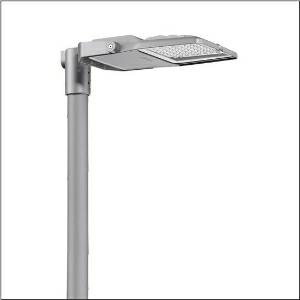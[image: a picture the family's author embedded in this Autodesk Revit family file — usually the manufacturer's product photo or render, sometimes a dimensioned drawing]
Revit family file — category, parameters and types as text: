
# Revit family: floodlight_fl_21_iq_mini___pl61_5xa7772c2c3a_f769
name_source: partatom
category: Lighting Fixtures
units: mm (PartAtom-declared; Revit-internal decimal feet)

## family parameters
Cut with Voids When Loaded = No
Host = Face
Light Source = No
Part Type = Normal
Room Calculation Point = No
Round Connector Dimension = Use Diameter
Shared = No

## types (1)
- --- (1 x LED, 11980 lm, 87.2 W, 3000K)
    Apparent Load = 87 VA
    CIE Flux Codes = 33 65 98 100 100
    Color Rendering = 70
    Color Temperature = 3000K
    Default Elevation = 1800 mm
    Description = Floodlight FL 21 iQ mini, floodlight, primary light control with lens, of PMMA, primary optical cover: protective disc, of toughened safety glass, transparent, light distribution: PL61, light emission: direct distribution, installation type: surface-mounted, LED, High Power LED, rated luminous flux: 11.980lm, luminous efficacy: 137lm/W, light colour: 730, colour temperature: 3000K, control gear: iQ Street-Remote/DALI, control: Auto-Match, Temp-Guard, Night-Set, Smart-Wire, Desk-Remote (wireless, voltage-free reading and setting of iQ features in the workshop via application-optimized NFC function/RFID function), optimised constant luminous flux control (CLO 2.0), Light-Fading, Lumen-Switch, with terminal, 6-pole, mains connection: 220..240V, AC, 50/60Hz, start of lifetime: 87W, end of service life: 92W, reduction: 40W, luminaire housing, of diecast aluminium, powder-coated, Siteco® metallic grey (DB 702S), corrosivity category C5 mid according to DIN EN ISO 12944, suitable for swimming pools, chlorine-resistant, sealing non-destructively replaceable, please order mast flange separately, mast bracket, of steel, galvanised, powder-coated, protection rating (complete): IP66, insulation class (complete): insulation class II (safety insulation), certification: CE, ENEC, VDE, protection symbol: D, impact resistance: IK08, permissible operating ambient temperature: -40..+40°C, permissible operating ambient temperature for outdoor applications: -40..+50°C, standard: DIN EN 12944, LABS conformity tested according to VDMA 24364:2018-05, packaging unit: 1 piece

Light Distribution: PL61
    Height = 70 mm
    Lamp = 1 x LED
    Lamp Light Flux = 11980 lm
    Lamp Power = 87.2 W
    Lamp count = 1
    Length = 485 mm
    Luminous efficacy = 137 lm/W
    Manufacturer = Siteco
    ModVariant = No
    Model = 5XA7772C2C3A
    Number of Poles = 1
    OnlyDefault = Yes
    Power Factor = 1
    Product Name = Floodlight FL 21 iQ mini | PL61
    Product group = floodlight | pylon annexe
    ProductGroupID = 6200
    Protection Class = Protection class II
    Protection Degree = IP 66
    RLX_Detail_Level = 1
    RLX_Emergency_Light_Flux = 0 lm
    RLX_Emergency_Type = 0
    RLX_Emergency_Type_DB = No
    RlxData = <blob elided: 101493 chars, md5=c12eae7b>
    Socket = socket
    Standby Power = 0 W
    System Light Flux = 11980 lm
    System Power = 87 W
    Type Comments = factory setting: luminous flux: 100 % | dim-lin: 254 | 456 mA
    Type Image = l_1007125.jpg
    URL = http://relux.com
    VarID = @adj_173044
    Voltage = 0 V
    Weight = 0.00 kg
    Width = 337 mm

## geometry (parser evidence)
native form markers: Blend x4, Sweep x12
no freeform markers — native parametric forms only
